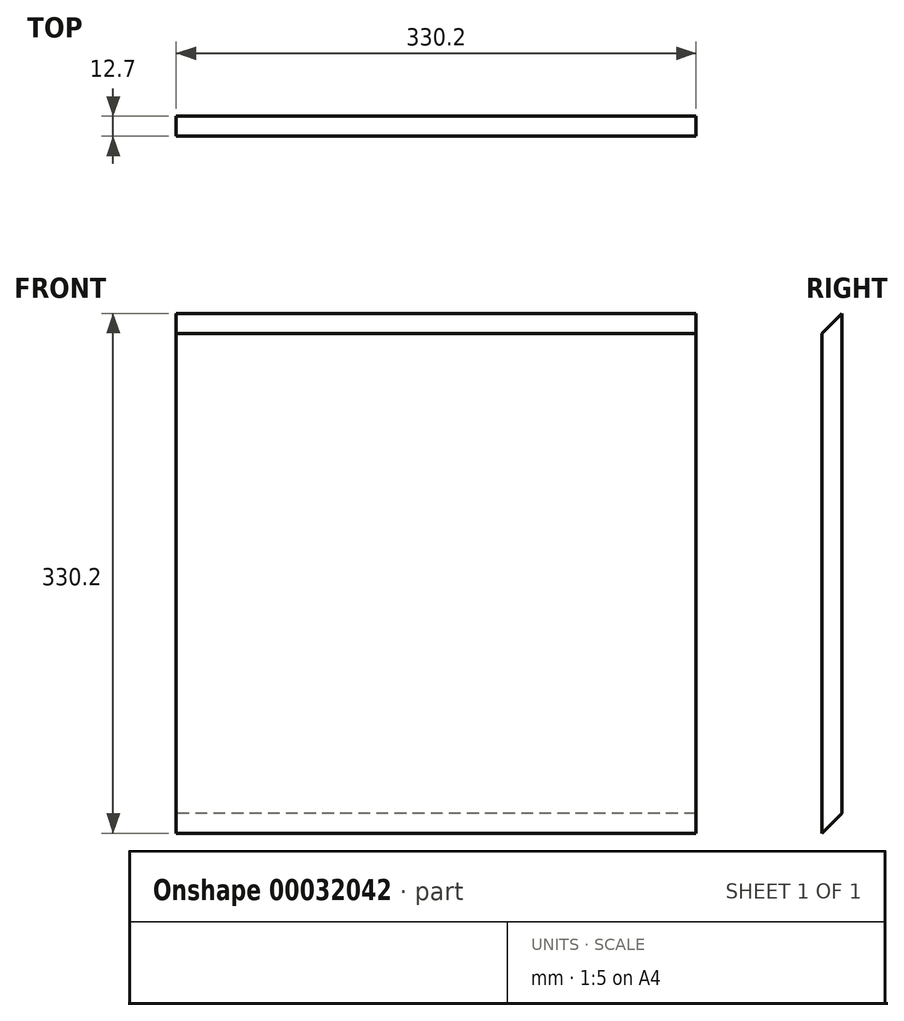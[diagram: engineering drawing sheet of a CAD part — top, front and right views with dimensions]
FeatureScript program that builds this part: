
annotation { "Feature Type Name" : "Feature", "Feature Type Description" : "" }
export const myFeature = defineFeature(function(context is Context, id is Id, definition is map)
    precondition{}
    {
        {
            var Q0;
            Q0=qCreatedBy(makeId("Top.planeOp"),FACE);
            var sketch = newSketch(context, id + "F0", { "sketchPlane" : qUnion([Q0])});
            skLineSegment(sketch, "E0.bottom", {"start": v(-32.51, 18.75) * mm, "end": v(297.69, 18.75) * mm});
            skLineSegment(sketch, "E0.top", {"start": v(-32.51, 31.45) * mm, "end": v(297.69, 31.45) * mm});
            skLineSegment(sketch, "E0.left", {"start": v(-32.51, 18.75) * mm, "end": v(-32.51, 31.45) * mm});
            skLineSegment(sketch, "E0.right", {"start": v(297.69, 18.75) * mm, "end": v(297.69, 31.45) * mm});
            skLineSegment(sketch, "E1", {"start": v(377.4, -52.7) * mm, "end": v(377.4, -37.1) * mm});
            skSolve(sketch);
        }
        {
            var Q0;
            Q0=makeQuery(id+"F0.imprint","IMPRINT",FACE,{"disambiguationData":[TD([[makeQuery(id+"F0.imprint","IMPRINT",EDGE,{"derivedFrom":sQuery(id+"F0.wireOp",EDGE,"E0.bottom")}),1.0]])]});
            var Q1;
            Q1=makeQuery(id+"F0.imprint","IMPRINT",FACE,{"disambiguationData":[TD([[makeQuery(id+"F0.imprint","IMPRINT",EDGE,{"derivedFrom":sQuery(id+"F0.wireOp",EDGE,"E0.right")}),-1.0]])]});
            var Q2;
            Q2=makeQuery(id+"F0.imprint","IMPRINT",FACE,{"disambiguationData":[TD([[makeQuery(id+"F0.imprint","IMPRINT",EDGE,{"derivedFrom":sQuery(id+"F0.wireOp",EDGE,"E0.left")}),1.0]])]});
            var Q3;
            {var subQ0=sQuery(id+"F0.wireOp",EDGE,"c61YTNUA-SIAm-74LC-GxgR-xpQFDATs0pW7");Q3=makeQuery(id+"F0.imprint","IMPRINT",FACE,{"disambiguationData":[TD([[makeQuery(id+"F0.imprint","IMPRINT",EDGE,{"derivedFrom":subQ0}),1.0]])]});}
            var Q4;
            {var subQ0=sQuery(id+"F0.wireOp",EDGE,"c61YTNUA-SIAm-74LC-GxgR-xpQFDATs0pW7");Q4=makeQuery(id+"F0.imprint","IMPRINT",FACE,{"disambiguationData":[TD([[makeQuery(id+"F0.imprint","IMPRINT",EDGE,{"derivedFrom":subQ0}),-1.0]])]});}
            extrude(context, id + "F1", {"entities" : qUnion([Q0, Q1, Q2, Q3, Q4]), "depth" : 330.2 * mm});
        }
        {
            var Q0;
            Q0=makeQuery(id+"F1.opExtrude","CAP_EDGE",EDGE,{"disambiguationData":[OSD([sQuery(id+"F0.wireOp",EDGE,"E0.top")])],"isStart":true});
            var Q1;
            Q1=makeQuery(id+"F1.opExtrude","CAP_EDGE",EDGE,{"disambiguationData":[OSD([sQuery(id+"F0.wireOp",EDGE,"E0.bottom")])],"isStart":false});
            var Q2;
            Q2=makeQuery(id+"F1.opExtrude","CAP_EDGE",EDGE,{"disambiguationData":[OSD([sQuery(id+"F0.wireOp",EDGE,"OikPGNP5-L4mw-s9MZ-n1SK-3jrxdiHjx4tQ")])],"isStart":false});
            var Q3;
            Q3=makeQuery(id+"F1.opExtrude","CAP_EDGE",EDGE,{"disambiguationData":[OSD([sQuery(id+"F0.wireOp",EDGE,"FORSKSXf-akUm-GuDD-UPAF-PIPNUNQk4dw9")])],"isStart":true});
            chamfer(context, id + "F2", {"entities" : qUnion([Q0, Q1, Q2, Q3]), "width" : 12.7 * mm, "tangentPropagation" : true});
        }
    });
